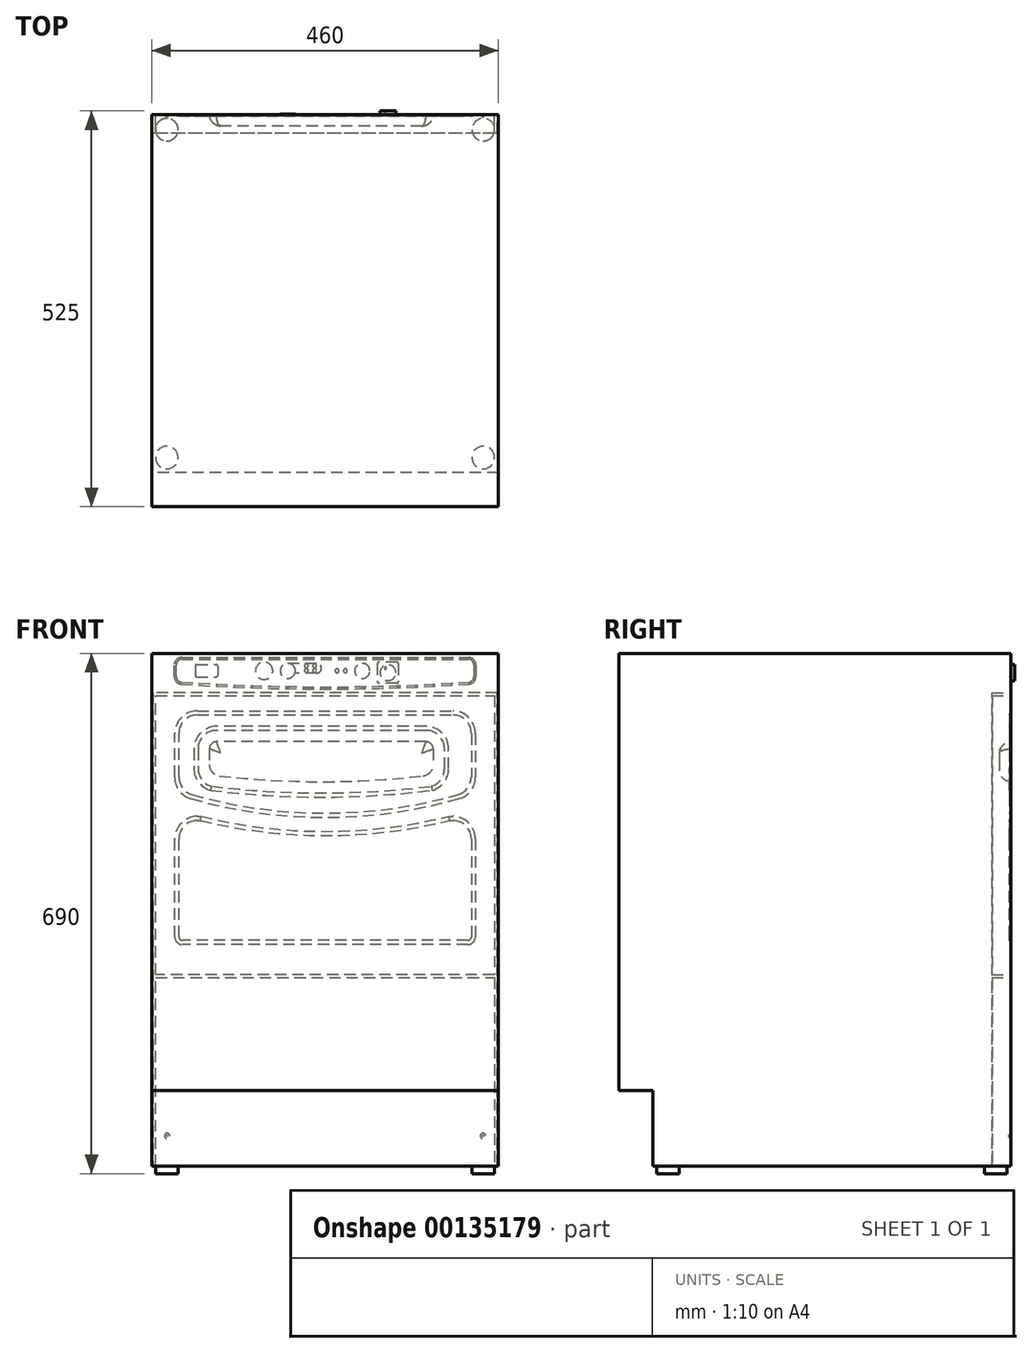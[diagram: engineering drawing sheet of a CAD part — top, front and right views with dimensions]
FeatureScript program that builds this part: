
annotation { "Feature Type Name" : "Feature", "Feature Type Description" : "" }
export const myFeature = defineFeature(function(context is Context, id is Id, definition is map)
    precondition{}
    {
        {
            var Q0;
            Q0=qCreatedBy(makeId("Right.planeOp"),FACE);
            var sketch = newSketch(context, id + "F0", { "sketchPlane" : qUnion([Q0])});
            skLineSegment(sketch, "E0", {"start": v(0, 0) * mm, "end": v(0, 680) * mm});
            skLineSegment(sketch, "E1", {"start": v(0, 680) * mm, "end": v(-520, 680) * mm});
            skLineSegment(sketch, "E2", {"start": v(-520, 680) * mm, "end": v(-520, 100) * mm});
            skLineSegment(sketch, "E3", {"start": v(-520, 100) * mm, "end": v(-475, 100) * mm});
            skLineSegment(sketch, "E4", {"start": v(-475, 100) * mm, "end": v(-475, 0) * mm});
            skLineSegment(sketch, "E5", {"start": v(-475, 0) * mm, "end": v(0, 0) * mm});
            skSolve(sketch);
        }
        {
            var Q0;
            Q0=qSketchRegion(id+"F0",true);
            extrude(context, id + "F1", {"entities" : qUnion([Q0]), "depth" : 460 * mm});
        }
        {
            var Q0;
            Q0=makeQuery(id+"F1.opExtrude","SWEPT_FACE",FACE,{"disambiguationData":[OSD([sQuery(id+"F0.wireOp",EDGE,"E5")])]});
            var sketch = newSketch(context, id + "F2", { "sketchPlane" : qUnion([Q0])});
            skCircle(sketch, "E6", {"center": v(440, 455) * mm, "radius": 15 * mm});
            skCircle(sketch, "E7", {"center": v(440, 20) * mm, "radius": 15 * mm});
            skCircle(sketch, "E8", {"center": v(20, 20) * mm, "radius": 15 * mm});
            skCircle(sketch, "E9", {"center": v(20, 455) * mm, "radius": 15 * mm});
            skSolve(sketch);
        }
        {
            var Q0;
            Q0=qSketchRegion(id+"F2",true);
            extrude(context, id + "F3", {"entities" : qUnion([Q0]), "operationType" : NewBodyOperationType.ADD, "depth" : 10 * mm});
        }
        {
            var Q0;
            Q0=makeQuery(id+"F1.opExtrude","SWEPT_FACE",FACE,{"disambiguationData":[OSD([sQuery(id+"F0.wireOp",EDGE,"E0")])]});
            var sketch = newSketch(context, id + "F4", { "sketchPlane" : qUnion([Q0])});
            skLineSegment(sketch, "E10", {"start": v(-458.5, 0) * mm, "end": v(-458.5, 628) * mm});
            skLineSegment(sketch, "E11", {"start": v(-458.5, 628) * mm, "end": v(-1.5, 628) * mm});
            skLineSegment(sketch, "E12", {"start": v(-1.5, 628) * mm, "end": v(-1.5, 0) * mm});
            skLineSegment(sketch, "E13", {"start": v(-1.5, 0) * mm, "end": v(-5.5, 0) * mm});
            skLineSegment(sketch, "E14", {"start": v(-5.5, 0) * mm, "end": v(-5.5, 250) * mm});
            skLineSegment(sketch, "E15", {"start": v(-5.5, 250) * mm, "end": v(-454.5, 250) * mm});
            skLineSegment(sketch, "E16", {"start": v(-454.5, 250) * mm, "end": v(-454.5, 0) * mm});
            skLineSegment(sketch, "E17", {"start": v(-454.5, 0) * mm, "end": v(-458.5, 0) * mm});
            skLineSegment(sketch, "E18", {"start": v(-454.5, 254) * mm, "end": v(-5.5, 254) * mm});
            skLineSegment(sketch, "E19", {"start": v(-5.5, 254) * mm, "end": v(-5.5, 624) * mm});
            skLineSegment(sketch, "E20", {"start": v(-5.5, 624) * mm, "end": v(-454.5, 624) * mm});
            skLineSegment(sketch, "E21", {"start": v(-454.5, 624) * mm, "end": v(-454.5, 254) * mm});
            skSolve(sketch);
        }
        {
            var Q0;
            Q0=qSketchRegion(id+"F4",true);
            extrude(context, id + "F5", {"entities" : qUnion([Q0]), "operationType" : NewBodyOperationType.REMOVE, "oppositeDirection" : true, "depth" : 25 * mm});
        }
        {
            var Q0;
            Q0=makeQuery(id+"F5.boolean.opBoolean","SPLIT",FACE,{"disambiguationData":[TD([makeQuery(id+"F5.opExtrude","SWEPT_FACE",FACE,{"disambiguationData":[OSD([sQuery(id+"F4.wireOp",EDGE,"E14")])]})])],"derivedFrom":makeQuery(id+"F1.opExtrude","SWEPT_FACE",FACE,{"disambiguationData":[OSD([sQuery(id+"F0.wireOp",EDGE,"E0")])]})});
            var sketch = newSketch(context, id + "F6", { "sketchPlane" : qUnion([Q0])});
            skCircle(sketch, "E22", {"center": v(-439.5, 40) * mm, "radius": 3.5 * mm});
            skCircle(sketch, "E23", {"center": v(-20.5, 40) * mm, "radius": 3.5 * mm});
            skSolve(sketch);
        }
        {
            var Q0;
            Q0=qSketchRegion(id+"F6",true);
            extrude(context, id + "F7", {"entities" : qUnion([Q0]), "operationType" : NewBodyOperationType.REMOVE, "oppositeDirection" : true, "depth" : 3 * mm, "hasDraft" : true, "draftAngle" : 45 * degree, "draftPullDirection" : true});
        }
        {
            var Q0;
            Q0=makeQuery(id+"F5.boolean.opBoolean","SPLIT",FACE,{"disambiguationData":[TD([makeQuery(id+"F5.opExtrude","SWEPT_FACE",FACE,{"disambiguationData":[OSD([sQuery(id+"F4.wireOp",EDGE,"E18")])]})])],"derivedFrom":makeQuery(id+"F1.opExtrude","SWEPT_FACE",FACE,{"disambiguationData":[OSD([sQuery(id+"F0.wireOp",EDGE,"E0")])]})});
            var sketch = newSketch(context, id + "F8", { "sketchPlane" : qUnion([Q0])});
            skLineSegment(sketch, "E24", {"start": v(-419.5, 294) * mm, "end": v(-40.5, 294) * mm});
            skLineSegment(sketch, "E25", {"start": v(-30.5, 304) * mm, "end": v(-30.5, 434) * mm});
            skLineSegment(sketch, "E26", {"start": v(-60.5, 464) * mm, "end": v(-65.5, 464) * mm});
            skLineSegment(sketch, "E27", {"start": v(-429.5, 304) * mm, "end": v(-429.5, 434) * mm});
            skLineSegment(sketch, "E28", {"start": v(-399.5, 464) * mm, "end": v(-394.5, 464) * mm});
            skArc(sketch, "E29", {"start": v(-394.5, 464) * mm, "mid": v(-230, 444) * mm, "end": v(-65.5, 464) * mm});
            skPoint(sketch, "E30.visualSharp", {"position": v(-429.5, 294) * mm});
            skArc(sketch, "E30.filletArc", {"start": v(-429.5, 304) * mm, "mid": v(-426.57, 296.93) * mm, "end": v(-419.5, 294) * mm});
            skPoint(sketch, "E31.visualSharp", {"position": v(-30.5, 294) * mm});
            skArc(sketch, "E31.filletArc", {"start": v(-40.5, 294) * mm, "mid": v(-33.43, 296.93) * mm, "end": v(-30.5, 304) * mm});
            skPoint(sketch, "E32.visualSharp", {"position": v(-30.5, 464) * mm});
            skArc(sketch, "E32.filletArc", {"start": v(-30.5, 434) * mm, "mid": v(-39.29, 455.21) * mm, "end": v(-60.5, 464) * mm});
            skPoint(sketch, "E33.visualSharp", {"position": v(-429.5, 464) * mm});
            skArc(sketch, "E33.filletArc", {"start": v(-399.5, 464) * mm, "mid": v(-420.71, 455.21) * mm, "end": v(-429.5, 434) * mm});
            skSolve(sketch);
        }
        {
            var Q0;
            Q0=qSketchRegion(id+"F8",true);
            extrude(context, id + "F9", {"entities" : qUnion([Q0]), "operationType" : NewBodyOperationType.REMOVE, "oppositeDirection" : true, "depth" : 2 * mm, "hasDraft" : true, "draftAngle" : 70 * degree, "draftPullDirection" : true});
        }
        {
            var Q0;
            Q0=makeQuery(id+"F5.boolean.opBoolean","SPLIT",FACE,{"disambiguationData":[TD([makeQuery(id+"F5.opExtrude","SWEPT_FACE",FACE,{"disambiguationData":[OSD([sQuery(id+"F4.wireOp",EDGE,"E18")])]})])],"derivedFrom":makeQuery(id+"F1.opExtrude","SWEPT_FACE",FACE,{"disambiguationData":[OSD([sQuery(id+"F0.wireOp",EDGE,"E0")])]})});
            var sketch = newSketch(context, id + "F10", { "sketchPlane" : qUnion([Q0])});
            skLineSegment(sketch, "E34", {"start": v(-429.5, 574) * mm, "end": v(-429.5, 516.27) * mm});
            skLineSegment(sketch, "E35", {"start": v(-399.5, 604) * mm, "end": v(-60.5, 604) * mm});
            skLineSegment(sketch, "E36", {"start": v(-30.5, 574) * mm, "end": v(-30.5, 516.27) * mm});
            skArc(sketch, "E37", {"start": v(-407.67, 487.4) * mm, "mid": v(-230, 462.74) * mm, "end": v(-52.33, 487.4) * mm});
            skPoint(sketch, "E38.visualSharp", {"position": v(-429.5, 604) * mm});
            skArc(sketch, "E38.filletArc", {"start": v(-399.5, 604) * mm, "mid": v(-420.71, 595.21) * mm, "end": v(-429.5, 574) * mm});
            skPoint(sketch, "E39.visualSharp", {"position": v(-30.5, 604) * mm});
            skArc(sketch, "E39.filletArc", {"start": v(-30.5, 574) * mm, "mid": v(-39.29, 595.21) * mm, "end": v(-60.5, 604) * mm});
            skPoint(sketch, "E40.visualSharp", {"position": v(-429.5, 494) * mm});
            skArc(sketch, "E40.filletArc", {"start": v(-429.5, 516.27) * mm, "mid": v(-423.43, 498.18) * mm, "end": v(-407.67, 487.4) * mm});
            skPoint(sketch, "E41.visualSharp", {"position": v(-30.5, 494) * mm});
            skArc(sketch, "E41.filletArc", {"start": v(-52.33, 487.4) * mm, "mid": v(-36.57, 498.18) * mm, "end": v(-30.5, 516.27) * mm});
            skSolve(sketch);
        }
        {
            var Q0;
            Q0=qSketchRegion(id+"F10",true);
            extrude(context, id + "F11", {"entities" : qUnion([Q0]), "operationType" : NewBodyOperationType.REMOVE, "oppositeDirection" : true, "depth" : 2 * mm, "hasDraft" : true, "draftAngle" : 70 * degree, "draftPullDirection" : true});
        }
        {
            var Q0;
            Q0=makeQuery(id+"F11.boolean.opBoolean","COPY",FACE,{"derivedFrom":makeQuery(id+"F11.opExtrude","CAP_FACE",FACE,{"disambiguationData":[OSD([sQuery(id+"F10.wireOp",EDGE,"E34"),sQuery(id+"F10.wireOp",EDGE,"E35"),sQuery(id+"F10.wireOp",EDGE,"E36"),sQuery(id+"F10.wireOp",EDGE,"E37"),sQuery(id+"F10.wireOp",EDGE,"E38.filletArc"),sQuery(id+"F10.wireOp",EDGE,"E39.filletArc"),sQuery(id+"F10.wireOp",EDGE,"E40.filletArc"),sQuery(id+"F10.wireOp",EDGE,"E41.filletArc")])],"isStart":false})});
            var sketch = newSketch(context, id + "F12", { "sketchPlane" : qUnion([Q0])});
            skLineSegment(sketch, "E42.bottom", {"start": v(-364, 583.5) * mm, "end": v(-86, 583.5) * mm});
            skLineSegment(sketch, "E42.left", {"start": v(-394, 553.5) * mm, "end": v(-394, 527.4) * mm});
            skLineSegment(sketch, "E42.right", {"start": v(-56, 553.5) * mm, "end": v(-56, 527.4) * mm});
            skPoint(sketch, "E43.visualSharp", {"position": v(-394, 508.02) * mm});
            skArc(sketch, "E43.filletArc", {"start": v(-394, 527.4) * mm, "mid": v(-387.9, 509.26) * mm, "end": v(-372.08, 498.5) * mm});
            skPoint(sketch, "E44.visualSharp", {"position": v(-394, 583.5) * mm});
            skArc(sketch, "E44.filletArc", {"start": v(-364, 583.5) * mm, "mid": v(-385.22, 574.72) * mm, "end": v(-394, 553.5) * mm});
            skPoint(sketch, "E45.visualSharp", {"position": v(-56, 583.5) * mm});
            skArc(sketch, "E45.filletArc", {"start": v(-56, 553.5) * mm, "mid": v(-64.78, 574.72) * mm, "end": v(-86, 583.5) * mm});
            skPoint(sketch, "E46.visualSharp", {"position": v(-56, 508.02) * mm});
            skArc(sketch, "E46.filletArc", {"start": v(-77.92, 498.5) * mm, "mid": v(-62.1, 509.26) * mm, "end": v(-56, 527.4) * mm});
            skArc(sketch, "E47", {"start": v(-372.08, 498.5) * mm, "mid": v(-225, 489.5) * mm, "end": v(-77.92, 498.5) * mm});
            skSolve(sketch);
        }
        {
            var Q0;
            Q0=qSketchRegion(id+"F12",true);
            extrude(context, id + "F13", {"entities" : qUnion([Q0]), "operationType" : NewBodyOperationType.ADD, "depth" : 2 * mm, "hasDraft" : true, "draftAngle" : 70 * degree, "draftPullDirection" : true});
        }
        {
            var Q0;
            {var subQ1=sQuery(id+"F0.wireOp",EDGE,"E1");var subQ5=sQuery(id+"F0.wireOp",EDGE,"E0");Q0=makeQuery(id+"F5.boolean.opBoolean","SPLIT",FACE,{"disambiguationData":[TD([makeQuery(id+"F1.opExtrude","SWEPT_FACE",FACE,{"disambiguationData":[OSD([subQ1])]})])],"derivedFrom":makeQuery(id+"F1.opExtrude","SWEPT_FACE",FACE,{"disambiguationData":[OSD([subQ5])]})});}
            var sketch = newSketch(context, id + "F14", { "sketchPlane" : qUnion([Q0])});
            skLineSegment(sketch, "E48.bottom", {"start": v(-420, 675) * mm, "end": v(-40, 675) * mm});
            skLineSegment(sketch, "E48.left", {"start": v(-430, 665) * mm, "end": v(-430, 649.34) * mm});
            skLineSegment(sketch, "E48.right", {"start": v(-30, 665) * mm, "end": v(-30, 649.34) * mm});
            skArc(sketch, "E49", {"start": v(-420.67, 639.36) * mm, "mid": v(-230, 633) * mm, "end": v(-39.33, 639.36) * mm});
            skPoint(sketch, "E50.visualSharp", {"position": v(-430, 675) * mm});
            skArc(sketch, "E50.filletArc", {"start": v(-420, 675) * mm, "mid": v(-427.07, 672.07) * mm, "end": v(-430, 665) * mm});
            skPoint(sketch, "E51.visualSharp", {"position": v(-30, 675) * mm});
            skArc(sketch, "E51.filletArc", {"start": v(-30, 665) * mm, "mid": v(-32.93, 672.07) * mm, "end": v(-40, 675) * mm});
            skPoint(sketch, "E52.visualSharp", {"position": v(-430, 640) * mm});
            skArc(sketch, "E52.filletArc", {"start": v(-430, 649.34) * mm, "mid": v(-427.3, 642.5) * mm, "end": v(-420.67, 639.36) * mm});
            skPoint(sketch, "E53.visualSharp", {"position": v(-30, 640) * mm});
            skArc(sketch, "E53.filletArc", {"start": v(-39.33, 639.36) * mm, "mid": v(-32.7, 642.5) * mm, "end": v(-30, 649.34) * mm});
            skSolve(sketch);
        }
        {
            var Q0;
            Q0=makeQuery(id+"F14.imprint","IMPRINT",FACE,{"disambiguationData":[TD([[makeQuery(id+"F14.imprint","IMPRINT",EDGE,{"derivedFrom":sQuery(id+"F14.wireOp",EDGE,"E48.bottom")}),-1.0]])]});
            extrude(context, id + "F15", {"entities" : qUnion([Q0]), "operationType" : NewBodyOperationType.REMOVE, "depth" : 1 * mm});
        }
        {
            var Q0;
            Q0=qSketchRegion(id+"F14",true);
            extrude(context, id + "F16", {"entities" : qUnion([Q0]), "operationType" : NewBodyOperationType.REMOVE, "oppositeDirection" : true, "depth" : 1.5 * mm, "hasDraft" : true, "draftAngle" : 60 * degree, "draftPullDirection" : true});
        }
        {
            var Q0;
            Q0=makeQuery(id+"F16.boolean.opBoolean","COPY",FACE,{"derivedFrom":makeQuery(id+"F16.opExtrude","CAP_FACE",FACE,{"disambiguationData":[OSD([sQuery(id+"F14.wireOp",EDGE,"E48.bottom"),sQuery(id+"F14.wireOp",EDGE,"E48.left"),sQuery(id+"F14.wireOp",EDGE,"E48.right"),sQuery(id+"F14.wireOp",EDGE,"E49"),sQuery(id+"F14.wireOp",EDGE,"E50.filletArc"),sQuery(id+"F14.wireOp",EDGE,"E51.filletArc"),sQuery(id+"F14.wireOp",EDGE,"E52.filletArc"),sQuery(id+"F14.wireOp",EDGE,"E53.filletArc")])],"isStart":false})});
            var sketch = newSketch(context, id + "F17", { "sketchPlane" : qUnion([Q0])});
            skLineSegment(sketch, "E54.bottom", {"start": v(-327.4, 668.6) * mm, "end": v(-299.4, 668.6) * mm});
            skLineSegment(sketch, "E54.top", {"start": v(-327.4, 640.6) * mm, "end": v(-299.4, 640.6) * mm});
            skLineSegment(sketch, "E54.left", {"start": v(-327.4, 668.6) * mm, "end": v(-327.4, 640.6) * mm});
            skLineSegment(sketch, "E54.right", {"start": v(-299.4, 668.6) * mm, "end": v(-299.4, 640.6) * mm});
            skSolve(sketch);
        }
        {
            var Q0;
            Q0=qSketchRegion(id+"F17",true);
            extrude(context, id + "F18", {"entities" : qUnion([Q0]), "depth" : 1.5 * mm});
        }
        {
            var Q0;
            Q0=makeQuery(id+"F18.opExtrude","SWEPT_EDGE",EDGE,{"disambiguationData":[OSD([sQuery(id+"F17.wireOp",EDGE,"E54.bottom"),sQuery(id+"F17.wireOp",EDGE,"E54.left")])]});
            var Q1;
            Q1=makeQuery(id+"F18.opExtrude","SWEPT_EDGE",EDGE,{"disambiguationData":[OSD([sQuery(id+"F17.wireOp",EDGE,"E54.bottom"),sQuery(id+"F17.wireOp",EDGE,"E54.right")])]});
            var Q2;
            Q2=makeQuery(id+"F18.opExtrude","SWEPT_EDGE",EDGE,{"disambiguationData":[OSD([sQuery(id+"F17.wireOp",EDGE,"E54.top"),sQuery(id+"F17.wireOp",EDGE,"E54.right")])]});
            var Q3;
            Q3=makeQuery(id+"F18.opExtrude","SWEPT_EDGE",EDGE,{"disambiguationData":[OSD([sQuery(id+"F17.wireOp",EDGE,"E54.top"),sQuery(id+"F17.wireOp",EDGE,"E54.left")])]});
            fillet(context, id + "F19", {"entities" : qUnion([Q0, Q1, Q2, Q3]), "radius" : 2 * mm, "tangentPropagation" : true, "allowEdgeOverflow" : false});
        }
        {
            var Q0;
            Q0=makeQuery(id+"F18.opExtrude","CAP_EDGE",EDGE,{"disambiguationData":[OSD([sQuery(id+"F17.wireOp",EDGE,"E54.left")])],"isStart":false});
            fillet(context, id + "F20", {"entities" : qUnion([Q0]), "radius" : 0.5 * mm, "tangentPropagation" : true, "allowEdgeOverflow" : false});
        }
        {
            var Q0;
            Q0=makeQuery(id+"F18.opExtrude","CAP_FACE",FACE,{"disambiguationData":[OSD([sQuery(id+"F17.wireOp",EDGE,"E54.bottom"),sQuery(id+"F17.wireOp",EDGE,"E54.top"),sQuery(id+"F17.wireOp",EDGE,"E54.left"),sQuery(id+"F17.wireOp",EDGE,"E54.right")])],"isStart":false});
            var sketch = newSketch(context, id + "F21", { "sketchPlane" : qUnion([Q0])});
            skCircle(sketch, "E55", {"center": v(-313.4, 654.6) * mm, "radius": 10.5 * mm});
            skPoint(sketch, "E55.centerSnap0", {"position": v(-313.4, 668.1) * mm});
            skPoint(sketch, "E55.centerSnap1", {"position": v(-326.9, 654.6) * mm});
            skSolve(sketch);
        }
        {
            var Q0;
            Q0=qSketchRegion(id+"F21",true);
            extrude(context, id + "F22", {"entities" : qUnion([Q0]), "depth" : 5 * mm});
        }
        {
            var Q0;
            Q0=makeQuery(id+"F22.opExtrude","CAP_FACE",FACE,{"disambiguationData":[OSD([sQuery(id+"F21.wireOp",EDGE,"E55")])],"isStart":false});
            var sketch = newSketch(context, id + "F23", { "sketchPlane" : qUnion([Q0])});
            skCircle(sketch, "E56", {"center": v(-309.9, 660.6) * mm, "radius": 1.5 * mm});
            skSolve(sketch);
        }
        {
            var Q0;
            Q0=qSketchRegion(id+"F23",true);
            extrude(context, id + "F24", {"entities" : qUnion([Q0]), "operationType" : NewBodyOperationType.REMOVE, "oppositeDirection" : true, "depth" : 1 * mm});
        }
        {
            var Q0;
            Q0=makeQuery(id+"F16.boolean.opBoolean","COPY",FACE,{"derivedFrom":makeQuery(id+"F16.opExtrude","CAP_FACE",FACE,{"disambiguationData":[OSD([sQuery(id+"F14.wireOp",EDGE,"E48.bottom"),sQuery(id+"F14.wireOp",EDGE,"E48.left"),sQuery(id+"F14.wireOp",EDGE,"E48.right"),sQuery(id+"F14.wireOp",EDGE,"E49"),sQuery(id+"F14.wireOp",EDGE,"E50.filletArc"),sQuery(id+"F14.wireOp",EDGE,"E51.filletArc"),sQuery(id+"F14.wireOp",EDGE,"E52.filletArc"),sQuery(id+"F14.wireOp",EDGE,"E53.filletArc")])],"isStart":false})});
            var sketch = newSketch(context, id + "F25", { "sketchPlane" : qUnion([Q0])});
            skLineSegment(sketch, "E57.bottom", {"start": v(-59.6, 665.17) * mm, "end": v(-85.6, 665.17) * mm});
            skLineSegment(sketch, "E57.top", {"start": v(-59.6, 649.17) * mm, "end": v(-85.6, 649.17) * mm});
            skLineSegment(sketch, "E57.left", {"start": v(-57.6, 663.17) * mm, "end": v(-57.6, 651.17) * mm});
            skLineSegment(sketch, "E57.right", {"start": v(-87.6, 663.17) * mm, "end": v(-87.6, 651.17) * mm});
            skPoint(sketch, "E58.visualSharp", {"position": v(-57.6, 665.17) * mm});
            skArc(sketch, "E58.filletArc", {"start": v(-57.6, 663.17) * mm, "mid": v(-58.18, 664.58) * mm, "end": v(-59.6, 665.17) * mm});
            skPoint(sketch, "E59.visualSharp", {"position": v(-57.6, 649.17) * mm});
            skArc(sketch, "E59.filletArc", {"start": v(-59.6, 649.17) * mm, "mid": v(-58.18, 649.76) * mm, "end": v(-57.6, 651.17) * mm});
            skPoint(sketch, "E60.visualSharp", {"position": v(-87.6, 649.17) * mm});
            skArc(sketch, "E60.filletArc", {"start": v(-87.6, 651.17) * mm, "mid": v(-87.01, 649.76) * mm, "end": v(-85.6, 649.17) * mm});
            skPoint(sketch, "E61.visualSharp", {"position": v(-87.6, 665.17) * mm});
            skArc(sketch, "E61.filletArc", {"start": v(-85.6, 665.17) * mm, "mid": v(-87.01, 664.58) * mm, "end": v(-87.6, 663.17) * mm});
            skSolve(sketch);
        }
        {
            var Q0;
            Q0=qSketchRegion(id+"F25",true);
            extrude(context, id + "F26", {"entities" : qUnion([Q0]), "depth" : 1.5 * mm});
        }
        {
            var Q0;
            Q0=makeQuery(id+"F26.opExtrude","CAP_EDGE",EDGE,{"disambiguationData":[OSD([sQuery(id+"F25.wireOp",EDGE,"E57.right")])],"isStart":false});
            fillet(context, id + "F27", {"entities" : qUnion([Q0]), "radius" : 1.5 * mm, "tangentPropagation" : true, "allowEdgeOverflow" : false});
        }
        {
            var Q0;
            Q0=makeQuery(id+"F16.boolean.opBoolean","COPY",FACE,{"derivedFrom":makeQuery(id+"F16.opExtrude","CAP_FACE",FACE,{"disambiguationData":[OSD([sQuery(id+"F14.wireOp",EDGE,"E48.bottom"),sQuery(id+"F14.wireOp",EDGE,"E48.left"),sQuery(id+"F14.wireOp",EDGE,"E48.right"),sQuery(id+"F14.wireOp",EDGE,"E49"),sQuery(id+"F14.wireOp",EDGE,"E50.filletArc"),sQuery(id+"F14.wireOp",EDGE,"E51.filletArc"),sQuery(id+"F14.wireOp",EDGE,"E52.filletArc"),sQuery(id+"F14.wireOp",EDGE,"E53.filletArc")])],"isStart":false})});
            var sketch = newSketch(context, id + "F28", { "sketchPlane" : qUnion([Q0])});
            skCircle(sketch, "E62", {"center": v(-149.1, 657) * mm, "radius": 11.5 * mm});
            skCircle(sketch, "E63", {"center": v(-180.6, 657) * mm, "radius": 10 * mm});
            skLineSegment(sketch, "E64", {"start": v(-180.6, 667) * mm, "end": v(-218.64, 667) * mm});
            skLineSegment(sketch, "E65", {"start": v(-225.14, 660.5) * mm, "end": v(-225.14, 660.5) * mm});
            skLineSegment(sketch, "E66", {"start": v(-218.64, 654) * mm, "end": v(-190.14, 654) * mm});
            skPoint(sketch, "E67.visualSharp", {"position": v(-225.14, 667) * mm});
            skArc(sketch, "E67.filletArc", {"start": v(-218.64, 667) * mm, "mid": v(-223.23, 665.1) * mm, "end": v(-225.14, 660.5) * mm});
            skPoint(sketch, "E68.visualSharp", {"position": v(-225.14, 654) * mm});
            skArc(sketch, "E68.filletArc", {"start": v(-225.14, 660.5) * mm, "mid": v(-223.23, 655.9) * mm, "end": v(-218.64, 654) * mm});
            skCircle(sketch, "E69", {"center": v(-216.14, 663.5) * mm, "radius": 2.5 * mm});
            skCircle(sketch, "E70", {"center": v(-205.14, 663.5) * mm, "radius": 2.5 * mm});
            skCircle(sketch, "E71", {"center": v(-205.14, 657.5) * mm, "radius": 2.5 * mm});
            skCircle(sketch, "E72", {"center": v(-216.14, 657.5) * mm, "radius": 2.5 * mm});
            skSolve(sketch);
        }
        {
            var Q0;
            {var subQ4=sQuery(id+"F14.wireOp",EDGE,"E50.filletArc");var subQ5=sQuery(id+"F14.wireOp",EDGE,"E48.right");var subQ6=sQuery(id+"F14.wireOp",EDGE,"E49");var subQ7=sQuery(id+"F14.wireOp",EDGE,"E48.bottom");var subQ8=sQuery(id+"F14.wireOp",EDGE,"E48.left");var subQ9=sQuery(id+"F14.wireOp",EDGE,"E53.filletArc");var subQ10=sQuery(id+"F14.wireOp",EDGE,"E51.filletArc");var subQ11=sQuery(id+"F14.wireOp",EDGE,"E52.filletArc");Q0=makeQuery(id+"FWKtfQyY8KCrMXJ_1.boolean.opBoolean","SPLIT",FACE,{"disambiguationData":[TD([makeQuery(id+"F16.boolean.opBoolean","COPY",FACE,{"derivedFrom":makeQuery(id+"F16.opExtrude","SWEPT_FACE",FACE,{"disambiguationData":[OSD([subQ7])]})})])],"derivedFrom":makeQuery(id+"F16.boolean.opBoolean","COPY",FACE,{"derivedFrom":makeQuery(id+"F16.opExtrude","CAP_FACE",FACE,{"disambiguationData":[OSD([subQ7,subQ8,subQ5,subQ6,subQ4,subQ10,subQ11,subQ9])],"isStart":false})})});}
            var sketch = newSketch(context, id + "F29", { "sketchPlane" : qUnion([Q0])});
            skCircle(sketch, "E73", {"center": v(-245.9, 657) * mm, "radius": 2.5 * mm});
            skCircle(sketch, "E74", {"center": v(-256.9, 657) * mm, "radius": 2.5 * mm});
            skCircle(sketch, "E75", {"center": v(-279.4, 657) * mm, "radius": 10 * mm});
            skSolve(sketch);
        }
        {
            var Q0;
            Q0=qSketchRegion(id+"F29",true);
            extrude(context, id + "F30", {"entities" : qUnion([Q0]), "operationType" : NewBodyOperationType.ADD, "depth" : 1 * mm});
        }
        {
            var Q0;
            {var subQ4=sQuery(id+"F14.wireOp",EDGE,"E50.filletArc");var subQ5=sQuery(id+"F14.wireOp",EDGE,"E48.right");var subQ6=sQuery(id+"F14.wireOp",EDGE,"E49");var subQ7=sQuery(id+"F14.wireOp",EDGE,"E48.bottom");var subQ8=sQuery(id+"F14.wireOp",EDGE,"E48.left");var subQ9=sQuery(id+"F14.wireOp",EDGE,"E53.filletArc");var subQ10=sQuery(id+"F14.wireOp",EDGE,"E51.filletArc");var subQ11=sQuery(id+"F14.wireOp",EDGE,"E52.filletArc");Q0=makeQuery(id+"FWKtfQyY8KCrMXJ_1.boolean.opBoolean","SPLIT",FACE,{"disambiguationData":[TD([makeQuery(id+"F16.boolean.opBoolean","COPY",FACE,{"derivedFrom":makeQuery(id+"F16.opExtrude","SWEPT_FACE",FACE,{"disambiguationData":[OSD([subQ7])]})})])],"derivedFrom":makeQuery(id+"F16.boolean.opBoolean","COPY",FACE,{"derivedFrom":makeQuery(id+"F16.opExtrude","CAP_FACE",FACE,{"disambiguationData":[OSD([subQ7,subQ8,subQ5,subQ6,subQ4,subQ10,subQ11,subQ9])],"isStart":false})})});}
            extrude(context, id + "F31", {"entities" : qUnion([Q0]), "depth" : 0.1 * mm});
        }
        {
            var Q0;
            {var subQ0=sQuery(id+"F28.wireOp",EDGE,"E63");var subQ1=makeQuery(id+"F28.imprint","INTERSECT",VERTEX,{"derivedFrom":[subQ0,sQuery(id+"F28.wireOp",EDGE,"E64")]});Q0=makeQuery(id+"F28.imprint","IMPRINT",FACE,{"disambiguationData":[TD([[makeQuery(id+"F28.imprint","IMPRINT",EDGE,{"disambiguationData":[TD([[subQ1,-1.0]])],"derivedFrom":subQ0}),1.0]])]});}
            extrude(context, id + "F32", {"entities" : qUnion([Q0]), "depth" : 2 * mm});
        }
        {
            var Q0;
            {var subQ1=sQuery(id+"F28.wireOp",EDGE,"E64");Q0=makeQuery(id+"F28.imprint","IMPRINT",FACE,{"disambiguationData":[TD([[makeQuery(id+"F28.imprint","IMPRINT",EDGE,{"derivedFrom":subQ1}),1.0]])]});}
            var Q1;
            Q1=makeQuery(id+"F28.imprint","IMPRINT",FACE,{"disambiguationData":[TD([[makeQuery(id+"F28.imprint","IMPRINT",EDGE,{"derivedFrom":sQuery(id+"F28.wireOp",EDGE,"E62")}),1.0]])]});
            extrude(context, id + "F33", {"entities" : qUnion([Q0, Q1]), "depth" : 1 * mm});
        }
        {
            var Q0;
            Q0=makeQuery(id+"F30.opExtrude","CAP_FACE",FACE,{"disambiguationData":[OSD([sQuery(id+"F29.wireOp",EDGE,"E75")])],"isStart":false});
            var Q1;
            Q1=makeQuery(id+"F30.opExtrude","CAP_FACE",FACE,{"disambiguationData":[OSD([sQuery(id+"F29.wireOp",EDGE,"E74")])],"isStart":false});
            var Q2;
            Q2=makeQuery(id+"F30.opExtrude","CAP_FACE",FACE,{"disambiguationData":[OSD([sQuery(id+"F29.wireOp",EDGE,"E73")])],"isStart":false});
            extrude(context, id + "F34", {"entities" : qUnion([Q0, Q1, Q2]), "depth" : 0.1 * mm});
        }
        {
            var Q0;
            Q0=makeQuery(id+"F13.opExtrude","CAP_FACE",FACE,{"disambiguationData":[OSD([sQuery(id+"F12.wireOp",EDGE,"E42.bottom"),sQuery(id+"F12.wireOp",EDGE,"E42.left"),sQuery(id+"F12.wireOp",EDGE,"E42.right"),sQuery(id+"F12.wireOp",EDGE,"E43.filletArc"),sQuery(id+"F12.wireOp",EDGE,"E44.filletArc"),sQuery(id+"F12.wireOp",EDGE,"E45.filletArc"),sQuery(id+"F12.wireOp",EDGE,"E46.filletArc"),sQuery(id+"F12.wireOp",EDGE,"E47")])],"isStart":false});
            var sketch = newSketch(context, id + "F35", { "sketchPlane" : qUnion([Q0])});
            skArc(sketch, "E76.0", {"start": v(-364, 563.01) * mm, "mid": v(-370.73, 560.23) * mm, "end": v(-373.51, 553.5) * mm});
            skLineSegment(sketch, "E76.1", {"start": v(-373.51, 553.5) * mm, "end": v(-373.51, 527.4) * mm});
            skLineSegment(sketch, "E76.2", {"start": v(-364, 563.01) * mm, "end": v(-86, 563.01) * mm});
            skArc(sketch, "E76.3", {"start": v(-373.51, 527.4) * mm, "mid": v(-371.9, 522.1) * mm, "end": v(-367.62, 518.6) * mm});
            skArc(sketch, "E76.4", {"start": v(-76.49, 553.5) * mm, "mid": v(-79.27, 560.23) * mm, "end": v(-86, 563.01) * mm});
            skLineSegment(sketch, "E76.5", {"start": v(-76.49, 553.5) * mm, "end": v(-76.49, 527.4) * mm});
            skArc(sketch, "E76.6", {"start": v(-82.38, 518.6) * mm, "mid": v(-78.1, 522.1) * mm, "end": v(-76.49, 527.4) * mm});
            skArc(sketch, "E76.7", {"start": v(-367.62, 518.6) * mm, "mid": v(-225, 509.99) * mm, "end": v(-82.38, 518.6) * mm});
            skSolve(sketch);
        }
        {
            var Q0;
            Q0 = qSketchRegion(id + "F35", true);
            extrude(context, id + "F36", {"entities" : qUnion([Q0]), "operationType" : NewBodyOperationType.REMOVE, "oppositeDirection" : true, "depth" : 15 * mm});
        }
        {
            var Q0;
            Q0=makeQuery(id+"F36.boolean.opBoolean","COPY",EDGE,{"derivedFrom":makeQuery(id+"F36.opExtrude","CAP_EDGE",EDGE,{"disambiguationData":[OSD([sQuery(id+"F35.wireOp",EDGE,"E76.2")])],"isStart":false})});
            fillet(context, id + "F37", {"entities" : qUnion([Q0]), "radius" : 15 * mm, "tangentPropagation" : true, "allowEdgeOverflow" : false});
        }
        {
            var Q0;
            Q0=makeQuery(id+"F36.boolean.opBoolean","COPY",EDGE,{"derivedFrom":makeQuery(id+"F36.opExtrude","CAP_EDGE",EDGE,{"disambiguationData":[OSD([sQuery(id+"F35.wireOp",EDGE,"E76.7")])],"isStart":false})});
            fillet(context, id + "F38", {"entities" : qUnion([Q0]), "radius" : 15 * mm, "tangentPropagation" : true, "allowEdgeOverflow" : false});
        }
    });
